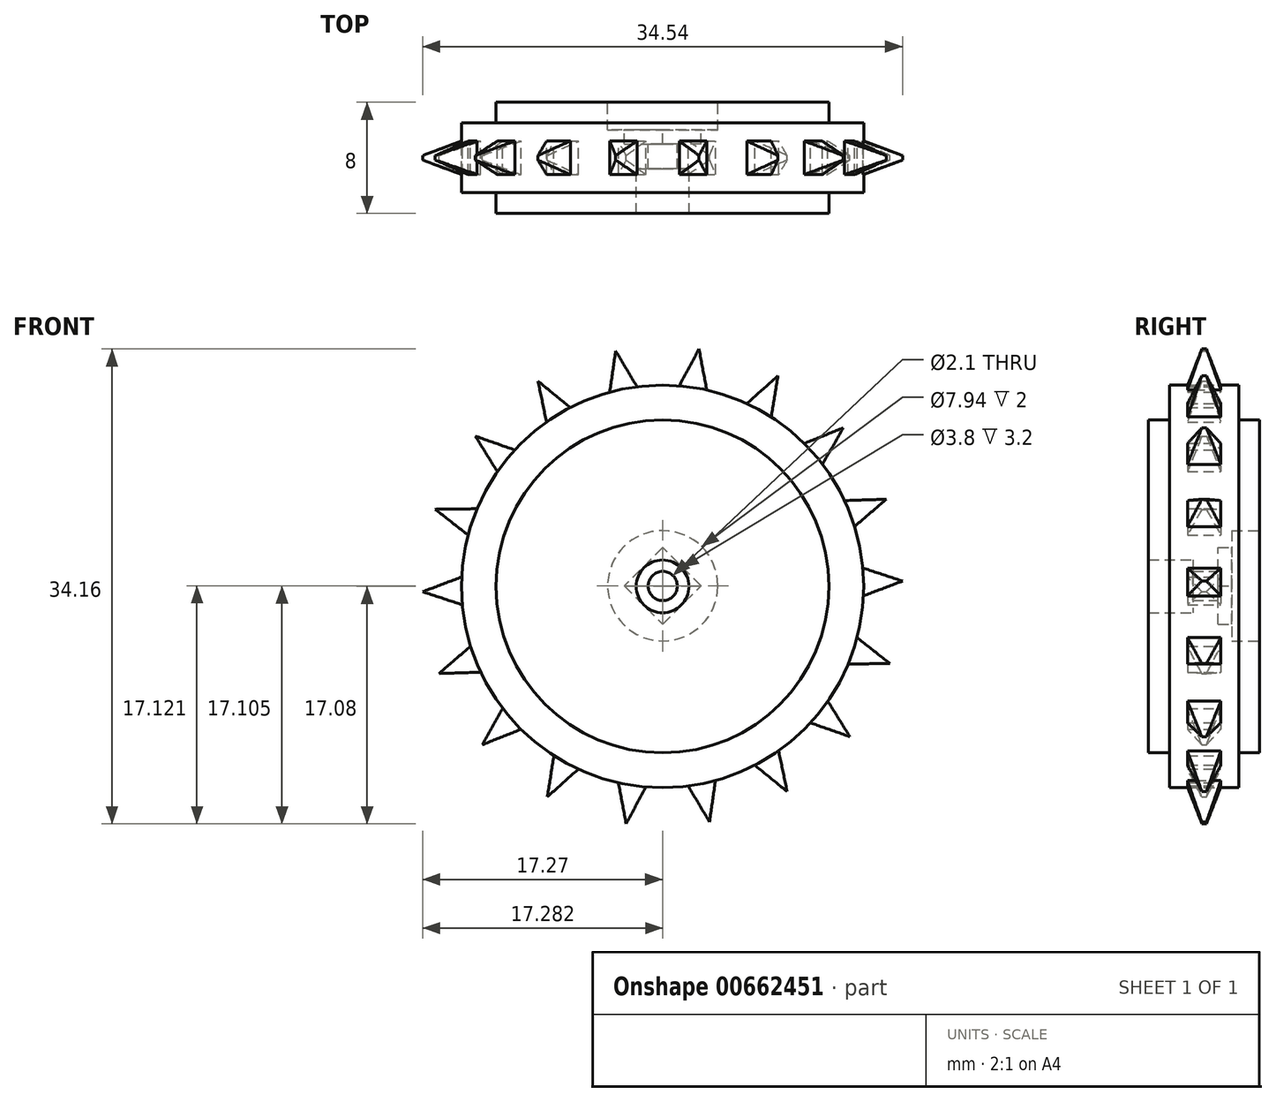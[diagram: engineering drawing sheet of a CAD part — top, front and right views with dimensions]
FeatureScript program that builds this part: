
annotation { "Feature Type Name" : "Feature", "Feature Type Description" : "" }
export const myFeature = defineFeature(function(context is Context, id is Id, definition is map)
    precondition{}
    {
        {
            var Q0;
            Q0=qCreatedBy(makeId("Front.planeOp"),FACE);
            var sketch = newSketch(context, id + "F0", { "sketchPlane" : qUnion([Q0])});
            skCircle(sketch, "E0.cCircle", {"center": v(0, 0) * mm, "radius": 17.01 * mm, "construction": true});
            skLineSegment(sketch, "E0.0", {"start": v(16.36, -5.55) * mm, "end": v(13.48, -10.8) * mm});
            skLineSegment(sketch, "E0.1", {"start": v(13.48, -10.8) * mm, "end": v(8.97, -14.77) * mm});
            skLineSegment(sketch, "E0.2", {"start": v(8.97, -14.77) * mm, "end": v(3.38, -16.94) * mm});
            skLineSegment(sketch, "E0.3", {"start": v(3.38, -16.94) * mm, "end": v(-2.62, -17.08) * mm});
            skLineSegment(sketch, "E0.4", {"start": v(-2.62, -17.08) * mm, "end": v(-8.3, -15.15) * mm});
            skLineSegment(sketch, "E0.5", {"start": v(-8.3, -15.15) * mm, "end": v(-12.98, -11.4) * mm});
            skLineSegment(sketch, "E0.6", {"start": v(-12.98, -11.4) * mm, "end": v(-16.1, -6.27) * mm});
            skLineSegment(sketch, "E0.7", {"start": v(-16.1, -6.27) * mm, "end": v(-17.27, -0.38) * mm});
            skLineSegment(sketch, "E0.8", {"start": v(-17.27, -0.38) * mm, "end": v(-16.36, 5.55) * mm});
            skLineSegment(sketch, "E0.9", {"start": v(-16.36, 5.55) * mm, "end": v(-13.48, 10.8) * mm});
            skLineSegment(sketch, "E0.10", {"start": v(-13.48, 10.8) * mm, "end": v(-8.97, 14.77) * mm});
            skLineSegment(sketch, "E0.11", {"start": v(-8.97, 14.77) * mm, "end": v(-3.38, 16.94) * mm});
            skLineSegment(sketch, "E0.12", {"start": v(-3.38, 16.94) * mm, "end": v(2.62, 17.08) * mm});
            skLineSegment(sketch, "E0.13", {"start": v(2.62, 17.08) * mm, "end": v(8.3, 15.15) * mm});
            skLineSegment(sketch, "E0.14", {"start": v(8.3, 15.15) * mm, "end": v(12.98, 11.4) * mm});
            skLineSegment(sketch, "E0.15", {"start": v(12.98, 11.4) * mm, "end": v(16.1, 6.27) * mm});
            skLineSegment(sketch, "E0.16", {"start": v(16.1, 6.27) * mm, "end": v(17.27, 0.38) * mm});
            skLineSegment(sketch, "E0.17", {"start": v(17.27, 0.38) * mm, "end": v(16.36, -5.55) * mm});
            skPoint(sketch, "E0.0.midPoint", {"position": v(14.92, -8.18) * mm});
            skLineSegment(sketch, "E1", {"start": v(-61.38, -2.75) * mm, "end": v(-43.67, -5.95) * mm});
            skLineSegment(sketch, "E2", {"start": v(-3.38, 16.94) * mm, "end": v(-2.83, 14.2) * mm, "construction": true});
            skLineSegment(sketch, "E3", {"start": v(-2.83, 14.2) * mm, "end": v(-2.34, 11.75) * mm, "construction": true});
            skLineSegment(sketch, "E4", {"start": v(-2.34, 11.75) * mm, "end": v(0, 0) * mm, "construction": true});
            skCircle(sketch, "E5", {"center": v(0, 0) * mm, "radius": 11.98 * mm});
            skCircle(sketch, "E6", {"center": v(0, 0) * mm, "radius": 14.48 * mm});
            skLineSegment(sketch, "E7", {"start": v(0, 0) * mm, "end": v(2.62, 17.08) * mm, "construction": true});
            skPoint(sketch, "E8", {"position": v(2.13, 13.85) * mm});
            skLineSegment(sketch, "E9", {"start": v(2.13, 13.85) * mm, "end": v(0.99, 14.03) * mm, "construction": true});
            skLineSegment(sketch, "E10", {"start": v(2.62, 17.08) * mm, "end": v(0.99, 14.03) * mm});
            skLineSegment(sketch, "E11.MirrorCS", {"start": v(2.62, 17.08) * mm, "end": v(3.26, 13.68) * mm});
            skLineSegment(sketch, "E12.14.0", {"start": v(16.7, 0.37) * mm, "end": v(13.41, 1.45) * mm});
            skPoint(sketch, "E13.0", {"position": v(0.01, 0.03) * mm});
            skCircle(sketch, "E14.cCircle", {"center": v(0.01, 0.03) * mm, "radius": 2.75 * mm, "construction": true});
            skLineSegment(sketch, "E14.0", {"start": v(-2.74, 0.03) * mm, "end": v(0.01, 2.78) * mm});
            skLineSegment(sketch, "E14.1", {"start": v(0.01, 2.78) * mm, "end": v(2.76, 0.03) * mm});
            skLineSegment(sketch, "E14.2", {"start": v(2.76, 0.03) * mm, "end": v(0.01, -2.73) * mm});
            skLineSegment(sketch, "E14.3", {"start": v(0.01, -2.73) * mm, "end": v(-2.74, 0.03) * mm});
            skCircle(sketch, "E15", {"center": v(0.01, 0.03) * mm, "radius": 1.05 * mm});
            skCircle(sketch, "E16", {"center": v(0.01, 0.03) * mm, "radius": 3.97 * mm});
            skLineSegment(sketch, "E17", {"start": v(2.13, 13.85) * mm, "end": v(2.75, 17.9) * mm});
            skLineSegment(sketch, "E18.1.0", {"start": v(-2.74, 13.75) * mm, "end": v(-3.87, 13.52) * mm, "construction": true});
            skPoint(sketch, "E18.1.1", {"position": v(-2.74, 13.75) * mm});
            skLineSegment(sketch, "E18.1.2", {"start": v(-3.38, 16.94) * mm, "end": v(-3.87, 13.52) * mm});
            skLineSegment(sketch, "E18.1.3", {"start": v(-3.38, 16.94) * mm, "end": v(-1.61, 13.97) * mm});
            skLineSegment(sketch, "E18.2.0", {"start": v(-7.28, 11.98) * mm, "end": v(-8.26, 11.38) * mm, "construction": true});
            skPoint(sketch, "E18.2.1", {"position": v(-7.28, 11.98) * mm});
            skLineSegment(sketch, "E18.2.2", {"start": v(-8.97, 14.77) * mm, "end": v(-8.26, 11.38) * mm});
            skLineSegment(sketch, "E18.2.3", {"start": v(-8.97, 14.77) * mm, "end": v(-6.3, 12.58) * mm});
            skLineSegment(sketch, "E18.3.0", {"start": v(-10.94, 8.77) * mm, "end": v(-11.66, 7.87) * mm, "construction": true});
            skPoint(sketch, "E18.3.1", {"position": v(-10.94, 8.77) * mm});
            skLineSegment(sketch, "E18.3.2", {"start": v(-13.48, 10.8) * mm, "end": v(-11.66, 7.87) * mm});
            skLineSegment(sketch, "E18.3.3", {"start": v(-13.48, 10.8) * mm, "end": v(-10.22, 9.67) * mm});
            skLineSegment(sketch, "E18.4.0", {"start": v(-13.28, 4.5) * mm, "end": v(-13.64, 3.41) * mm, "construction": true});
            skPoint(sketch, "E18.4.1", {"position": v(-13.28, 4.5) * mm});
            skLineSegment(sketch, "E18.4.2", {"start": v(-16.36, 5.55) * mm, "end": v(-13.64, 3.41) * mm});
            skLineSegment(sketch, "E18.4.3", {"start": v(-16.36, 5.55) * mm, "end": v(-12.9, 5.59) * mm});
            skLineSegment(sketch, "E18.5.0", {"start": v(-14.01, -0.31) * mm, "end": v(-13.99, -1.46) * mm, "construction": true});
            skPoint(sketch, "E18.5.1", {"position": v(-14.01, -0.31) * mm});
            skLineSegment(sketch, "E18.5.2", {"start": v(-17.27, -0.38) * mm, "end": v(-13.99, -1.46) * mm});
            skLineSegment(sketch, "E18.5.3", {"start": v(-17.27, -0.38) * mm, "end": v(-14.04, 0.84) * mm});
            skLineSegment(sketch, "E18.6.0", {"start": v(-13.06, -5.09) * mm, "end": v(-12.64, -6.16) * mm, "construction": true});
            skPoint(sketch, "E18.6.1", {"position": v(-13.06, -5.09) * mm});
            skLineSegment(sketch, "E18.6.2", {"start": v(-16.1, -6.27) * mm, "end": v(-12.64, -6.16) * mm});
            skLineSegment(sketch, "E18.6.3", {"start": v(-16.1, -6.27) * mm, "end": v(-13.48, -4.01) * mm});
            skLineSegment(sketch, "E18.7.0", {"start": v(-10.53, -9.25) * mm, "end": v(-9.78, -10.11) * mm, "construction": true});
            skPoint(sketch, "E18.7.1", {"position": v(-10.53, -9.25) * mm});
            skLineSegment(sketch, "E18.7.2", {"start": v(-12.98, -11.4) * mm, "end": v(-9.78, -10.11) * mm});
            skLineSegment(sketch, "E18.7.3", {"start": v(-12.98, -11.4) * mm, "end": v(-11.3, -8.38) * mm});
            skLineSegment(sketch, "E18.8.0", {"start": v(-6.74, -12.3) * mm, "end": v(-5.73, -12.84) * mm, "construction": true});
            skPoint(sketch, "E18.8.1", {"position": v(-6.74, -12.3) * mm});
            skLineSegment(sketch, "E18.8.2", {"start": v(-8.3, -15.15) * mm, "end": v(-5.73, -12.84) * mm});
            skLineSegment(sketch, "E18.8.3", {"start": v(-8.3, -15.15) * mm, "end": v(-7.75, -11.74) * mm});
            skLineSegment(sketch, "E18.9.0", {"start": v(-2.13, -13.85) * mm, "end": v(-0.99, -14.03) * mm, "construction": true});
            skPoint(sketch, "E18.9.1", {"position": v(-2.13, -13.85) * mm});
            skLineSegment(sketch, "E18.9.2", {"start": v(-2.62, -17.08) * mm, "end": v(-0.99, -14.03) * mm});
            skLineSegment(sketch, "E18.9.3", {"start": v(-2.62, -17.08) * mm, "end": v(-3.26, -13.68) * mm});
            skLineSegment(sketch, "E18.10.0", {"start": v(2.74, -13.75) * mm, "end": v(3.87, -13.52) * mm, "construction": true});
            skPoint(sketch, "E18.10.1", {"position": v(2.74, -13.75) * mm});
            skLineSegment(sketch, "E18.10.2", {"start": v(3.38, -16.94) * mm, "end": v(3.87, -13.52) * mm});
            skLineSegment(sketch, "E18.10.3", {"start": v(3.38, -16.94) * mm, "end": v(1.61, -13.97) * mm});
            skLineSegment(sketch, "E18.11.0", {"start": v(7.28, -11.98) * mm, "end": v(8.26, -11.38) * mm, "construction": true});
            skPoint(sketch, "E18.11.1", {"position": v(7.28, -11.98) * mm});
            skLineSegment(sketch, "E18.11.2", {"start": v(8.97, -14.77) * mm, "end": v(8.26, -11.38) * mm});
            skLineSegment(sketch, "E18.11.3", {"start": v(8.97, -14.77) * mm, "end": v(6.3, -12.58) * mm});
            skLineSegment(sketch, "E18.12.0", {"start": v(10.94, -8.77) * mm, "end": v(11.66, -7.87) * mm, "construction": true});
            skPoint(sketch, "E18.12.1", {"position": v(10.94, -8.77) * mm});
            skLineSegment(sketch, "E18.12.2", {"start": v(13.48, -10.8) * mm, "end": v(11.66, -7.87) * mm});
            skLineSegment(sketch, "E18.12.3", {"start": v(13.48, -10.8) * mm, "end": v(10.22, -9.67) * mm});
            skLineSegment(sketch, "E18.13.0", {"start": v(13.28, -4.5) * mm, "end": v(13.64, -3.41) * mm, "construction": true});
            skPoint(sketch, "E18.13.1", {"position": v(13.28, -4.5) * mm});
            skLineSegment(sketch, "E18.13.2", {"start": v(16.36, -5.55) * mm, "end": v(13.64, -3.41) * mm});
            skLineSegment(sketch, "E18.13.3", {"start": v(16.36, -5.55) * mm, "end": v(12.9, -5.59) * mm});
            skLineSegment(sketch, "E18.14.0", {"start": v(14.01, 0.31) * mm, "end": v(13.99, 1.46) * mm, "construction": true});
            skPoint(sketch, "E18.14.1", {"position": v(14.01, 0.31) * mm});
            skLineSegment(sketch, "E18.14.2", {"start": v(17.27, 0.38) * mm, "end": v(13.99, 1.46) * mm});
            skLineSegment(sketch, "E18.14.3", {"start": v(17.27, 0.38) * mm, "end": v(14.04, -0.84) * mm});
            skLineSegment(sketch, "E18.15.0", {"start": v(13.06, 5.09) * mm, "end": v(12.64, 6.16) * mm, "construction": true});
            skPoint(sketch, "E18.15.1", {"position": v(13.06, 5.09) * mm});
            skLineSegment(sketch, "E18.15.2", {"start": v(16.1, 6.27) * mm, "end": v(12.64, 6.16) * mm});
            skLineSegment(sketch, "E18.15.3", {"start": v(16.1, 6.27) * mm, "end": v(13.48, 4.01) * mm});
            skLineSegment(sketch, "E18.16.0", {"start": v(10.53, 9.25) * mm, "end": v(9.78, 10.11) * mm, "construction": true});
            skPoint(sketch, "E18.16.1", {"position": v(10.53, 9.25) * mm});
            skLineSegment(sketch, "E18.16.2", {"start": v(12.98, 11.4) * mm, "end": v(9.78, 10.11) * mm});
            skLineSegment(sketch, "E18.16.3", {"start": v(12.98, 11.4) * mm, "end": v(11.3, 8.38) * mm});
            skLineSegment(sketch, "E18.17.0", {"start": v(6.74, 12.3) * mm, "end": v(5.73, 12.84) * mm, "construction": true});
            skPoint(sketch, "E18.17.1", {"position": v(6.74, 12.3) * mm});
            skLineSegment(sketch, "E18.17.2", {"start": v(8.3, 15.15) * mm, "end": v(5.73, 12.84) * mm});
            skLineSegment(sketch, "E18.17.3", {"start": v(8.3, 15.15) * mm, "end": v(7.75, 11.74) * mm});
            skSolve(sketch);
        }
        {
            var Q0;
            Q0=makeQuery(id+"F0.imprint","IMPRINT",FACE,{"disambiguationData":[TD([[makeQuery(id+"F0.imprint","IMPRINT",EDGE,{"derivedFrom":sQuery(id+"F0.wireOp",EDGE,"E5")}),-1.0]])]});
            var Q1;
            {var subQ0=sQuery(id+"F0.wireOp",EDGE,"E12.7.1");var subQ1=sQuery(id+"F0.wireOp",EDGE,"E6");var subQ2=makeQuery(id+"F0.imprint","INTERSECT",VERTEX,{"derivedFrom":[subQ1,subQ0]});Q1=makeQuery(id+"F0.imprint","IMPRINT",FACE,{"disambiguationData":[TD([[makeQuery(id+"F0.imprint","IMPRINT",EDGE,{"disambiguationData":[TD([[subQ2,-1.0]])],"derivedFrom":subQ1}),-1.0]])]});}
            var Q2;
            {var subQ0=sQuery(id+"F0.wireOp",EDGE,"E12.8.1");var subQ1=sQuery(id+"F0.wireOp",EDGE,"E6");var subQ2=makeQuery(id+"F0.imprint","INTERSECT",VERTEX,{"derivedFrom":[subQ1,subQ0]});Q2=makeQuery(id+"F0.imprint","IMPRINT",FACE,{"disambiguationData":[TD([[makeQuery(id+"F0.imprint","IMPRINT",EDGE,{"disambiguationData":[TD([[subQ2,-1.0]])],"derivedFrom":subQ1}),-1.0]])]});}
            var Q3;
            {var subQ0=sQuery(id+"F0.wireOp",EDGE,"E12.9.1");var subQ1=sQuery(id+"F0.wireOp",EDGE,"E6");var subQ2=makeQuery(id+"F0.imprint","INTERSECT",VERTEX,{"derivedFrom":[subQ1,subQ0]});Q3=makeQuery(id+"F0.imprint","IMPRINT",FACE,{"disambiguationData":[TD([[makeQuery(id+"F0.imprint","IMPRINT",EDGE,{"disambiguationData":[TD([[subQ2,-1.0]])],"derivedFrom":subQ1}),-1.0]])]});}
            var Q4;
            {var subQ0=sQuery(id+"F0.wireOp",EDGE,"E12.10.1");var subQ1=sQuery(id+"F0.wireOp",EDGE,"E6");var subQ2=makeQuery(id+"F0.imprint","INTERSECT",VERTEX,{"derivedFrom":[subQ1,subQ0]});Q4=makeQuery(id+"F0.imprint","IMPRINT",FACE,{"disambiguationData":[TD([[makeQuery(id+"F0.imprint","IMPRINT",EDGE,{"disambiguationData":[TD([[subQ2,-1.0]])],"derivedFrom":subQ1}),-1.0]])]});}
            var Q5;
            {var subQ0=sQuery(id+"F0.wireOp",EDGE,"E12.11.1");var subQ1=sQuery(id+"F0.wireOp",EDGE,"E6");var subQ2=makeQuery(id+"F0.imprint","INTERSECT",VERTEX,{"derivedFrom":[subQ1,subQ0]});Q5=makeQuery(id+"F0.imprint","IMPRINT",FACE,{"disambiguationData":[TD([[makeQuery(id+"F0.imprint","IMPRINT",EDGE,{"disambiguationData":[TD([[subQ2,-1.0]])],"derivedFrom":subQ1}),-1.0]])]});}
            var Q6;
            {var subQ0=sQuery(id+"F0.wireOp",EDGE,"E12.12.1");var subQ1=sQuery(id+"F0.wireOp",EDGE,"E6");var subQ2=makeQuery(id+"F0.imprint","INTERSECT",VERTEX,{"derivedFrom":[subQ1,subQ0]});Q6=makeQuery(id+"F0.imprint","IMPRINT",FACE,{"disambiguationData":[TD([[makeQuery(id+"F0.imprint","IMPRINT",EDGE,{"disambiguationData":[TD([[subQ2,-1.0]])],"derivedFrom":subQ1}),-1.0]])]});}
            var Q7;
            {var subQ0=sQuery(id+"F0.wireOp",EDGE,"E12.13.1");var subQ1=sQuery(id+"F0.wireOp",EDGE,"E6");var subQ2=makeQuery(id+"F0.imprint","INTERSECT",VERTEX,{"derivedFrom":[subQ1,subQ0]});Q7=makeQuery(id+"F0.imprint","IMPRINT",FACE,{"disambiguationData":[TD([[makeQuery(id+"F0.imprint","IMPRINT",EDGE,{"disambiguationData":[TD([[subQ2,-1.0]])],"derivedFrom":subQ1}),-1.0]])]});}
            var Q8;
            Q8=makeQuery(id+"F0.imprint","IMPRINT",FACE,{"disambiguationData":[TD([[makeQuery(id+"F0.imprint","IMPRINT",EDGE,{"derivedFrom":sQuery(id+"F0.wireOp",EDGE,"E5")}),1.0]])]});
            var Q9;
            {var subQ0=sQuery(id+"F0.wireOp",EDGE,"E12.14.0");var subQ1=sQuery(id+"F0.wireOp",EDGE,"E6");var subQ2=makeQuery(id+"F0.imprint","INTERSECT",VERTEX,{"derivedFrom":[subQ1,subQ0]});Q9=makeQuery(id+"F0.imprint","IMPRINT",FACE,{"disambiguationData":[TD([[makeQuery(id+"F0.imprint","IMPRINT",EDGE,{"disambiguationData":[TD([[subQ2,1.0]])],"derivedFrom":subQ1}),-1.0]])]});}
            var Q10;
            {var subQ0=sQuery(id+"F0.wireOp",EDGE,"E12.15.1");var subQ1=sQuery(id+"F0.wireOp",EDGE,"E6");var subQ2=makeQuery(id+"F0.imprint","INTERSECT",VERTEX,{"derivedFrom":[subQ1,subQ0]});Q10=makeQuery(id+"F0.imprint","IMPRINT",FACE,{"disambiguationData":[TD([[makeQuery(id+"F0.imprint","IMPRINT",EDGE,{"disambiguationData":[TD([[subQ2,-1.0]])],"derivedFrom":subQ1}),-1.0]])]});}
            var Q11;
            {var subQ0=sQuery(id+"F0.wireOp",EDGE,"E12.16.1");var subQ1=sQuery(id+"F0.wireOp",EDGE,"E6");var subQ2=makeQuery(id+"F0.imprint","INTERSECT",VERTEX,{"derivedFrom":[subQ1,subQ0]});Q11=makeQuery(id+"F0.imprint","IMPRINT",FACE,{"disambiguationData":[TD([[makeQuery(id+"F0.imprint","IMPRINT",EDGE,{"disambiguationData":[TD([[subQ2,-1.0]])],"derivedFrom":subQ1}),-1.0]])]});}
            var Q12;
            {var subQ0=sQuery(id+"F0.wireOp",EDGE,"E12.17.1");var subQ1=sQuery(id+"F0.wireOp",EDGE,"E6");var subQ2=makeQuery(id+"F0.imprint","INTERSECT",VERTEX,{"derivedFrom":[subQ1,subQ0]});Q12=makeQuery(id+"F0.imprint","IMPRINT",FACE,{"disambiguationData":[TD([[makeQuery(id+"F0.imprint","IMPRINT",EDGE,{"disambiguationData":[TD([[subQ2,-1.0]])],"derivedFrom":subQ1}),-1.0]])]});}
            var Q13;
            {var subQ0=sQuery(id+"F0.wireOp",EDGE,"E11.MirrorCS");var subQ1=sQuery(id+"F0.wireOp",EDGE,"E6");var subQ2=makeQuery(id+"F0.imprint","INTERSECT",VERTEX,{"derivedFrom":[subQ1,subQ0]});Q13=makeQuery(id+"F0.imprint","IMPRINT",FACE,{"disambiguationData":[TD([[makeQuery(id+"F0.imprint","IMPRINT",EDGE,{"disambiguationData":[TD([[subQ2,-1.0]])],"derivedFrom":subQ1}),-1.0]])]});}
            var Q14;
            {var subQ0=sQuery(id+"F0.wireOp",EDGE,"E12.1.1");var subQ1=sQuery(id+"F0.wireOp",EDGE,"E6");var subQ2=makeQuery(id+"F0.imprint","INTERSECT",VERTEX,{"derivedFrom":[subQ1,subQ0]});Q14=makeQuery(id+"F0.imprint","IMPRINT",FACE,{"disambiguationData":[TD([[makeQuery(id+"F0.imprint","IMPRINT",EDGE,{"disambiguationData":[TD([[subQ2,-1.0]])],"derivedFrom":subQ1}),-1.0]])]});}
            var Q15;
            {var subQ0=sQuery(id+"F0.wireOp",EDGE,"E12.2.1");var subQ1=sQuery(id+"F0.wireOp",EDGE,"E6");var subQ2=makeQuery(id+"F0.imprint","INTERSECT",VERTEX,{"derivedFrom":[subQ1,subQ0]});Q15=makeQuery(id+"F0.imprint","IMPRINT",FACE,{"disambiguationData":[TD([[makeQuery(id+"F0.imprint","IMPRINT",EDGE,{"disambiguationData":[TD([[subQ2,-1.0]])],"derivedFrom":subQ1}),-1.0]])]});}
            var Q16;
            {var subQ0=sQuery(id+"F0.wireOp",EDGE,"E12.3.1");var subQ1=sQuery(id+"F0.wireOp",EDGE,"E6");var subQ2=makeQuery(id+"F0.imprint","INTERSECT",VERTEX,{"derivedFrom":[subQ1,subQ0]});Q16=makeQuery(id+"F0.imprint","IMPRINT",FACE,{"disambiguationData":[TD([[makeQuery(id+"F0.imprint","IMPRINT",EDGE,{"disambiguationData":[TD([[subQ2,-1.0]])],"derivedFrom":subQ1}),-1.0]])]});}
            var Q17;
            {var subQ0=sQuery(id+"F0.wireOp",EDGE,"E12.4.1");var subQ1=sQuery(id+"F0.wireOp",EDGE,"E6");var subQ2=makeQuery(id+"F0.imprint","INTERSECT",VERTEX,{"derivedFrom":[subQ1,subQ0]});Q17=makeQuery(id+"F0.imprint","IMPRINT",FACE,{"disambiguationData":[TD([[makeQuery(id+"F0.imprint","IMPRINT",EDGE,{"disambiguationData":[TD([[subQ2,-1.0]])],"derivedFrom":subQ1}),-1.0]])]});}
            var Q18;
            {var subQ0=sQuery(id+"F0.wireOp",EDGE,"E12.5.1");var subQ1=sQuery(id+"F0.wireOp",EDGE,"E6");var subQ2=makeQuery(id+"F0.imprint","INTERSECT",VERTEX,{"derivedFrom":[subQ1,subQ0]});Q18=makeQuery(id+"F0.imprint","IMPRINT",FACE,{"disambiguationData":[TD([[makeQuery(id+"F0.imprint","IMPRINT",EDGE,{"disambiguationData":[TD([[subQ2,-1.0]])],"derivedFrom":subQ1}),-1.0]])]});}
            var Q19;
            {var subQ0=sQuery(id+"F0.wireOp",EDGE,"E12.6.1");var subQ1=sQuery(id+"F0.wireOp",EDGE,"E6");var subQ2=makeQuery(id+"F0.imprint","INTERSECT",VERTEX,{"derivedFrom":[subQ1,subQ0]});Q19=makeQuery(id+"F0.imprint","IMPRINT",FACE,{"disambiguationData":[TD([[makeQuery(id+"F0.imprint","IMPRINT",EDGE,{"disambiguationData":[TD([[subQ2,-1.0]])],"derivedFrom":subQ1}),-1.0]])]});}
            var Q20;
            {var subQ0=sQuery(id+"F0.wireOp",EDGE,"E17");var subQ1=sQuery(id+"F0.wireOp",EDGE,"E6");var subQ2=makeQuery(id+"F0.imprint","INTERSECT",VERTEX,{"derivedFrom":[subQ1,subQ0]});Q20=makeQuery(id+"F0.imprint","IMPRINT",FACE,{"disambiguationData":[TD([[makeQuery(id+"F0.imprint","IMPRINT",EDGE,{"disambiguationData":[TD([[subQ2,-1.0]])],"derivedFrom":subQ1}),-1.0]])]});}
            var Q21;
            {var subQ0=sQuery(id+"F0.wireOp",EDGE,"E6");var subQ1=makeQuery(id+"F0.imprint","IMPRINT",VERTEX,{"derivedFrom":subQ0});Q21=makeQuery(id+"F0.imprint","IMPRINT",FACE,{"disambiguationData":[TD([[makeQuery(id+"F0.imprint","IMPRINT",EDGE,{"disambiguationData":[TD([[subQ1,-1.0]])],"derivedFrom":subQ0}),-1.0]])]});}
            extrude(context, id + "F1", {"entities" : qUnion([Q0, Q1, Q2, Q3, Q4, Q5, Q6, Q7, Q8, Q9, Q10, Q11, Q12, Q13, Q14, Q15, Q16, Q17, Q18, Q19, Q20, Q21]), "endBound" : BoundingType.SYMMETRIC, "depth" : 2.4 * mm, "offsetDistance" : 25 * mm});
        }
        {
            var Q0;
            Q0=makeQuery(id+"F0.imprint","IMPRINT",FACE,{"disambiguationData":[TD([[makeQuery(id+"F0.imprint","IMPRINT",EDGE,{"derivedFrom":sQuery(id+"F0.wireOp",EDGE,"E5")}),-1.0]])]});
            extrude(context, id + "F2", {"entities" : qUnion([Q0]), "operationType" : NewBodyOperationType.ADD, "endBound" : BoundingType.SYMMETRIC, "depth" : 5 * mm, "offsetDistance" : 25 * mm});
        }
        {
            var Q0;
            Q0=makeQuery(id+"F0.imprint","IMPRINT",FACE,{"disambiguationData":[TD([[makeQuery(id+"F0.imprint","IMPRINT",EDGE,{"derivedFrom":sQuery(id+"F0.wireOp",EDGE,"E5")}),1.0]])]});
            var Q1;
            Q1=makeQuery(id+"F0.imprint","IMPRINT",FACE,{"disambiguationData":[TD([[makeQuery(id+"F0.imprint","IMPRINT",EDGE,{"derivedFrom":sQuery(id+"F0.wireOp",EDGE,"f1872843-3049-4890-8a67-7aa9caa9baa1.0")}),-1.0]])]});
            var Q2;
            Q2=makeQuery(id+"F0.imprint","IMPRINT",FACE,{"disambiguationData":[TD([[makeQuery(id+"F0.imprint","IMPRINT",EDGE,{"derivedFrom":sQuery(id+"F0.wireOp",EDGE,"E14.0")}),1.0]])]});
            var Q3;
            Q3=makeQuery(id+"F0.imprint","IMPRINT",FACE,{"disambiguationData":[TD([[makeQuery(id+"F0.imprint","IMPRINT",EDGE,{"derivedFrom":sQuery(id+"F0.wireOp",EDGE,"E14.0")}),-1.0]])]});
            extrude(context, id + "F3", {"entities" : qUnion([Q0, Q1, Q2, Q3]), "operationType" : NewBodyOperationType.ADD, "endBound" : BoundingType.SYMMETRIC, "depth" : 8 * mm, "offsetDistance" : 25 * mm});
        }
        {
            var Q0;
            Q0=makeQuery(id+"F3.opExtrude","CAP_FACE",FACE,{"disambiguationData":[OSD([sQuery(id+"F0.wireOp",EDGE,"E5"),sQuery(id+"F0.wireOp",EDGE,"E15")])],"isStart":true});
            var sketch = newSketch(context, id + "F4", { "sketchPlane" : qUnion([Q0])});
            skPoint(sketch, "E19.0", {"position": v(-0.01, 0.04) * mm});
            skCircle(sketch, "E20.cCircle", {"center": v(-0.01, 0.04) * mm, "radius": 2.75 * mm, "construction": true});
            skLineSegment(sketch, "E20.0", {"start": v(-2.76, 0.04) * mm, "end": v(-0.01, 2.8) * mm});
            skLineSegment(sketch, "E20.1", {"start": v(-0.01, 2.8) * mm, "end": v(2.74, 0.04) * mm});
            skLineSegment(sketch, "E20.2", {"start": v(2.74, 0.04) * mm, "end": v(-0.01, -2.71) * mm});
            skLineSegment(sketch, "E20.3", {"start": v(-0.01, -2.71) * mm, "end": v(-2.76, 0.04) * mm});
            skCircle(sketch, "E21", {"center": v(-0.01, 0.04) * mm, "radius": 1 * mm});
            skCircle(sketch, "E22", {"center": v(-0.01, 0.04) * mm, "radius": 3.97 * mm});
            skSolve(sketch);
        }
        {
            var Q0;
            Q0=makeQuery(id+"F4.imprint","IMPRINT",FACE,{"disambiguationData":[TD([[makeQuery(id+"F4.imprint","IMPRINT",EDGE,{"derivedFrom":sQuery(id+"F4.wireOp",EDGE,"E20.0")}),1.0]])]});
            extrude(context, id + "F5", {"entities" : qUnion([Q0]), "operationType" : NewBodyOperationType.REMOVE, "oppositeDirection" : true, "depth" : 2 * mm, "offsetDistance" : 25 * mm});
        }
        {
            var Q0;
            {var subQ0=sQuery(id+"F0.wireOp",EDGE,"E15");Q0=makeQuery(id+"F5.boolean.opBoolean","SPLIT",FACE,{"disambiguationData":[TD([makeQuery(id+"F3.opExtrude","SWEPT_FACE",FACE,{"disambiguationData":[OSD([subQ0])]})])],"derivedFrom":makeQuery(id+"F3.opExtrude","CAP_FACE",FACE,{"disambiguationData":[OSD([sQuery(id+"F0.wireOp",EDGE,"E5"),subQ0])],"isStart":true})});}
            extrude(context, id + "F6", {"entities" : qUnion([Q0]), "operationType" : NewBodyOperationType.REMOVE, "oppositeDirection" : true, "depth" : 3 * mm, "offsetDistance" : 25 * mm});
        }
        {
            var Q0;
            Q0=sQuery(id+"F0.wireOp",EDGE,"E17");
            extrude(context, id + "F7", {"bodyType" : ToolBodyType.SURFACE, "surfaceEntities" : qUnion([Q0]), "endBound" : BoundingType.SYMMETRIC, "depth" : 8 * mm, "offsetDistance" : 25 * mm});
        }
        {
            var Q0;
            Q0=makeQuery(id+"F7.opExtrude","SWEPT_FACE",FACE,{"disambiguationData":[OSD([sQuery(id+"F0.wireOp",EDGE,"E17")])]});
            var sketch = newSketch(context, id + "F8", { "sketchPlane" : qUnion([Q0])});
            skLineSegment(sketch, "E23.0", {"start": v(1.2, 17.28) * mm, "end": v(1.2, 14.44) * mm});
            skLineSegment(sketch, "E23.1", {"start": v(-1.2, 17.28) * mm, "end": v(-1.2, 14.44) * mm});
            skLineSegment(sketch, "E23.2", {"start": v(-1.2, 17.28) * mm, "end": v(0, 17.28) * mm});
            skPoint(sketch, "E23.3", {"position": v(1.2, 14.48) * mm});
            skPoint(sketch, "E23.4", {"position": v(-1.2, 14.48) * mm});
            skPoint(sketch, "E24", {"position": v(0, 17.28) * mm});
            skLineSegment(sketch, "E25", {"start": v(0, 17.28) * mm, "end": v(1.2, 17.28) * mm});
            skPoint(sketch, "E26", {"position": v(0.16, 17.28) * mm});
            skLineSegment(sketch, "E27", {"start": v(0.16, 17.28) * mm, "end": v(1.2, 14.48) * mm});
            skLineSegment(sketch, "E28", {"start": v(0, 17.05) * mm, "end": v(0, 13.55) * mm, "construction": true});
            skLineSegment(sketch, "E29.MirrorCS", {"start": v(-0.16, 17.28) * mm, "end": v(-1.2, 14.48) * mm});
            skPoint(sketch, "E30", {"position": v(0, 0) * mm});
            skLineSegment(sketch, "E31", {"start": v(0, 0) * mm, "end": v(3.84, 0) * mm, "construction": true});
            skSolve(sketch);
        }
        {
            var Q0;
            {var subQ3=sQuery(id+"F8.wireOp",EDGE,"E29.MirrorCS");Q0=makeQuery(id+"F8.imprint","IMPRINT",FACE,{"disambiguationData":[TD([[makeQuery(id+"F8.imprint","IMPRINT",EDGE,{"derivedFrom":subQ3}),-1.0]])]});}
            var Q1;
            {var subQ3=sQuery(id+"F8.wireOp",EDGE,"E27");Q1=makeQuery(id+"F8.imprint","IMPRINT",FACE,{"disambiguationData":[TD([[makeQuery(id+"F8.imprint","IMPRINT",EDGE,{"derivedFrom":subQ3}),1.0]])]});}
            var Q2;
            Q2=sQuery(id+"F8.wireOp",EDGE,"E31");
            revolve(context, id + "F9", {"operationType" : NewBodyOperationType.REMOVE, "entities" : qUnion([Q0, Q1]), "axis" : qUnion([Q2]), "revolveType" : RevolveType.FULL, "oppositeDirection" : true});
        }
        {
            var Q0;
            Q0=makeQuery(id+"F6.boolean.opBoolean","COPY",FACE,{"derivedFrom":makeQuery(id+"F6.opExtrude","CAP_FACE",FACE,{"disambiguationData":[OSD([sQuery(id+"F0.wireOp",EDGE,"E5"),sQuery(id+"F0.wireOp",EDGE,"E15")])],"isStart":false})});
            var sketch = newSketch(context, id + "F10", { "sketchPlane" : qUnion([Q0])});
            skPoint(sketch, "E32.0", {"position": v(0, 0) * mm});
            skCircle(sketch, "E33", {"center": v(0, 0) * mm, "radius": 1.9 * mm});
            skSolve(sketch);
        }
        {
            var Q0;
            Q0=makeQuery(id+"F10.imprint","IMPRINT",FACE,{"disambiguationData":[TD([[makeQuery(id+"F10.imprint","IMPRINT",EDGE,{"derivedFrom":sQuery(id+"F10.wireOp",EDGE,"E33")}),1.0]])]});
            extrude(context, id + "F11", {"entities" : qUnion([Q0]), "operationType" : NewBodyOperationType.REMOVE, "oppositeDirection" : true, "depth" : 6.97 * mm, "offsetDistance" : 25 * mm, "hasSecondDirection" : true, "secondDirectionOppositeDirection" : true, "secondDirectionDepth" : 1.8 * mm});
        }
    });
